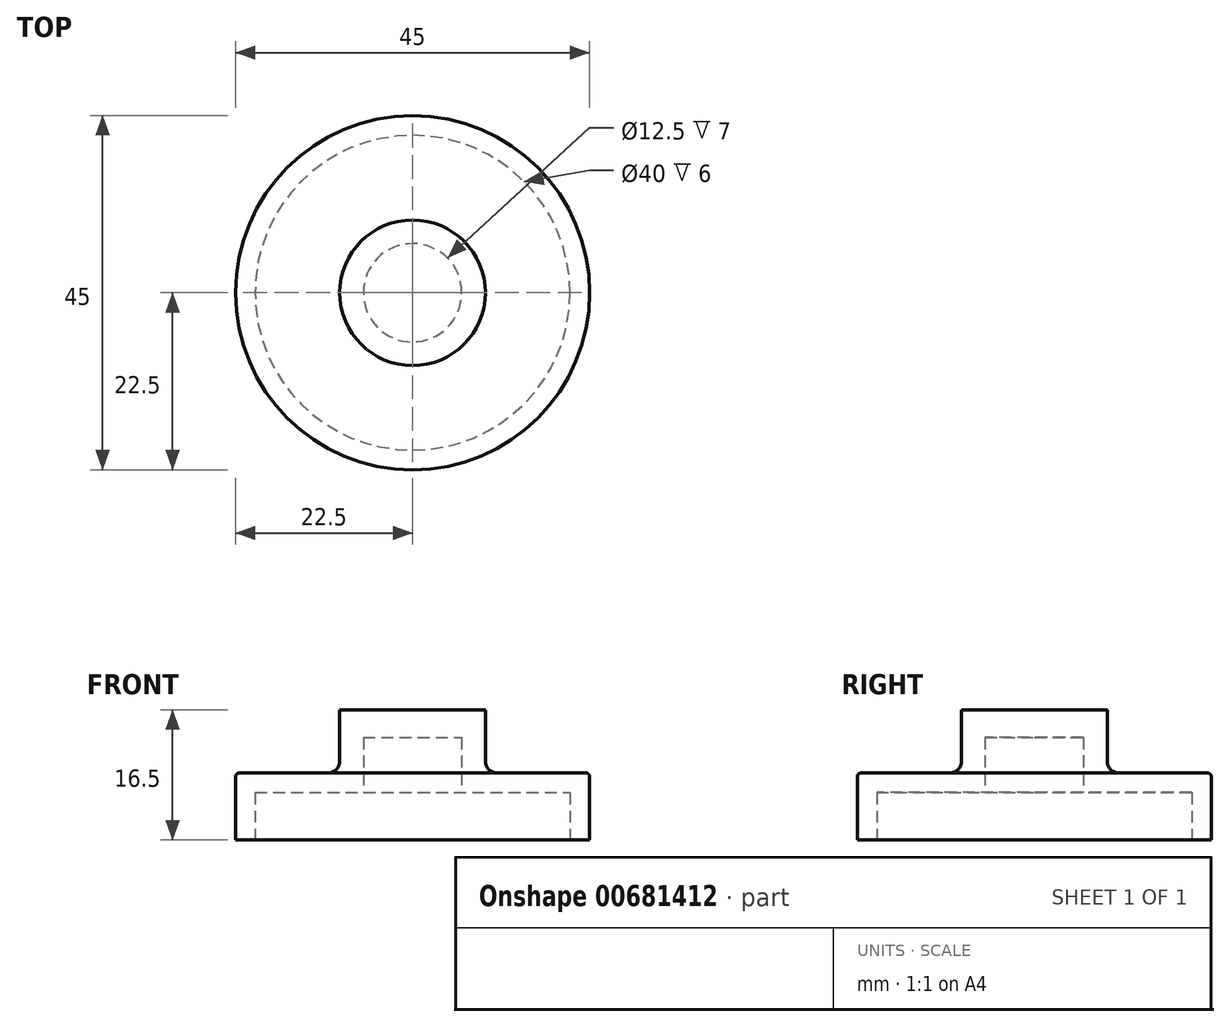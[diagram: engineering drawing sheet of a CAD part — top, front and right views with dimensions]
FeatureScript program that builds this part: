
annotation { "Feature Type Name" : "Feature", "Feature Type Description" : "" }
export const myFeature = defineFeature(function(context is Context, id is Id, definition is map)
    precondition{}
    {
        {
            var Q0;
            Q0=qCreatedBy(makeId("Front.planeOp"),FACE);
            var sketch = newSketch(context, id + "F0", { "sketchPlane" : qUnion([Q0])});
            skLineSegment(sketch, "E0", {"start": v(0, 13) * mm, "end": v(6.25, 13) * mm});
            skLineSegment(sketch, "E1", {"start": v(6.25, 13) * mm, "end": v(6.25, 6) * mm});
            skLineSegment(sketch, "E2", {"start": v(6.25, 6) * mm, "end": v(20, 6) * mm});
            skLineSegment(sketch, "E3", {"start": v(20, 0) * mm, "end": v(22.5, 0) * mm});
            skLineSegment(sketch, "E4", {"start": v(22.5, 0) * mm, "end": v(22.5, 8.5) * mm});
            skLineSegment(sketch, "E5", {"start": v(22.5, 8.5) * mm, "end": v(9.25, 8.5) * mm});
            skLineSegment(sketch, "E6", {"start": v(9.25, 16.5) * mm, "end": v(9.25, 8.5) * mm});
            skLineSegment(sketch, "E7", {"start": v(9.25, 16.5) * mm, "end": v(0, 16.5) * mm});
            skLineSegment(sketch, "E8", {"start": v(0, 13) * mm, "end": v(0, 16.5) * mm});
            skLineSegment(sketch, "E9", {"start": v(20, 0) * mm, "end": v(20, 6) * mm});
            skSolve(sketch);
        }
        {
            var Q0;
            Q0=makeQuery(id+"F0.imprint","IMPRINT",FACE,{"disambiguationData":[TD([[makeQuery(id+"F0.imprint","IMPRINT",EDGE,{"derivedFrom":sQuery(id+"F0.wireOp",EDGE,"E0")}),1.0]])]});
            var Q1;
            Q1=sQuery(id+"F0.wireOp",EDGE,"E8");
            revolve(context, id + "F1", {"entities" : qUnion([Q0]), "axis" : qUnion([Q1]), "revolveType" : RevolveType.FULL});
        }
        {
            var Q0;
            Q0=makeQuery(id+"F1.opRevolve","SWEPT_EDGE",EDGE,{"disambiguationData":[OSD([sQuery(id+"F0.wireOp",EDGE,"E5"),sQuery(id+"F0.wireOp",EDGE,"E6")])]});
            fillet(context, id + "F2", {"entities" : qUnion([Q0]), "radius" : 1.5 * mm, "tangentPropagation" : true, "allowEdgeOverflow" : false});
        }
        {
            var Q0;
            Q0=makeQuery(id+"F1.opRevolve","SWEPT_EDGE",EDGE,{"disambiguationData":[OSD([sQuery(id+"F0.wireOp",EDGE,"E4"),sQuery(id+"F0.wireOp",EDGE,"E5")])]});
            fillet(context, id + "F3", {"entities" : qUnion([Q0]), "radius" : 0.5 * mm, "tangentPropagation" : true, "allowEdgeOverflow" : false});
        }
    });
